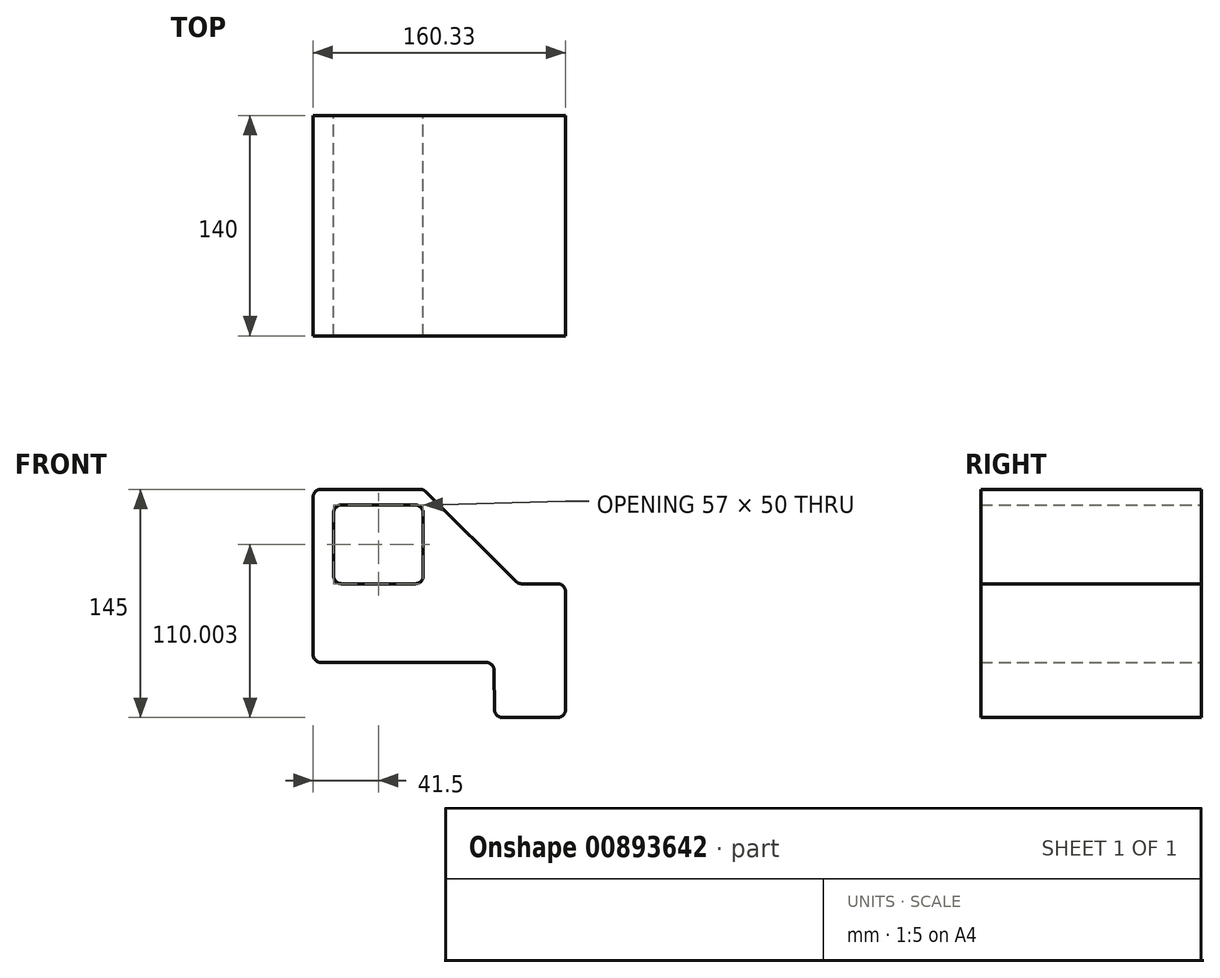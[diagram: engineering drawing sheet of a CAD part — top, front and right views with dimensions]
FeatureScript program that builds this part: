
annotation { "Feature Type Name" : "Feature", "Feature Type Description" : "" }
export const myFeature = defineFeature(function(context is Context, id is Id, definition is map)
    precondition{}
    {
        {
            var Q0;
            Q0=qCreatedBy(makeId("Front.planeOp"),FACE);
            var sketch = newSketch(context, id + "F0", { "sketchPlane" : qUnion([Q0])});
            skLineSegment(sketch, "E0", {"start": v(-70, 32.02) * mm, "end": v(45, 32.02) * mm});
            skLineSegment(sketch, "E1", {"start": v(45.33, -2.98) * mm, "end": v(90.33, -2.98) * mm});
            skLineSegment(sketch, "E2", {"start": v(90.33, -2.98) * mm, "end": v(90.33, 82.02) * mm});
            skLineSegment(sketch, "E3", {"start": v(90.33, 82.02) * mm, "end": v(60.33, 82.02) * mm});
            skLineSegment(sketch, "E4", {"start": v(60.33, 82.02) * mm, "end": v(0, 142.02) * mm});
            skLineSegment(sketch, "E5", {"start": v(0, 142.02) * mm, "end": v(-70, 142.02) * mm});
            skLineSegment(sketch, "E6", {"start": v(-70, 142.02) * mm, "end": v(-70, 32.02) * mm});
            skLineSegment(sketch, "E7", {"start": v(45, 32.02) * mm, "end": v(45.33, -2.98) * mm});
            skSolve(sketch);
        }
        {
            var Q0;
            Q0 = qSketchRegion(id + "F0", true);
            extrude(context, id + "F1", {"entities" : qUnion([Q0]), "endBound" : BoundingType.SYMMETRIC, "depth" : 140 * mm, "offsetDistance" : 25 * mm});
        }
        {
            var Q0;
            Q0=makeQuery(id+"F1.opExtrude","CAP_FACE",FACE,{"disambiguationData":[OSD([sQuery(id+"F0.wireOp",EDGE,"E0"),sQuery(id+"F0.wireOp",EDGE,"E1"),sQuery(id+"F0.wireOp",EDGE,"E2"),sQuery(id+"F0.wireOp",EDGE,"E3"),sQuery(id+"F0.wireOp",EDGE,"E4"),sQuery(id+"F0.wireOp",EDGE,"E5"),sQuery(id+"F0.wireOp",EDGE,"E6"),sQuery(id+"F0.wireOp",EDGE,"E7")])],"isStart":true});
            var sketch = newSketch(context, id + "F2", { "sketchPlane" : qUnion([Q0])});
            skLineSegment(sketch, "E8.bottom", {"start": v(5, 132.02) * mm, "end": v(52, 132.02) * mm});
            skLineSegment(sketch, "E8.top", {"start": v(5, 82.02) * mm, "end": v(52, 82.02) * mm});
            skLineSegment(sketch, "E8.left", {"start": v(0, 127.02) * mm, "end": v(0, 87.02) * mm});
            skLineSegment(sketch, "E8.right", {"start": v(57, 127.02) * mm, "end": v(57, 87.02) * mm});
            skPoint(sketch, "E9.visualSharp", {"position": v(0, 132.02) * mm});
            skArc(sketch, "E9.filletArc", {"start": v(5, 132.02) * mm, "mid": v(1.46, 130.56) * mm, "end": v(0, 127.02) * mm});
            skPoint(sketch, "E10.visualSharp", {"position": v(57, 132.02) * mm});
            skArc(sketch, "E10.filletArc", {"start": v(57, 127.02) * mm, "mid": v(55.54, 130.56) * mm, "end": v(52, 132.02) * mm});
            skPoint(sketch, "E11.visualSharp", {"position": v(57, 82.02) * mm});
            skArc(sketch, "E11.filletArc", {"start": v(52, 82.02) * mm, "mid": v(55.54, 83.49) * mm, "end": v(57, 87.02) * mm});
            skPoint(sketch, "E12.visualSharp", {"position": v(0, 82.02) * mm});
            skArc(sketch, "E12.filletArc", {"start": v(0, 87.02) * mm, "mid": v(1.46, 83.49) * mm, "end": v(5, 82.02) * mm});
            skSolve(sketch);
        }
        {
            var Q0;
            Q0=makeQuery(id+"F2.imprint","IMPRINT",FACE,{"disambiguationData":[TD([[makeQuery(id+"F2.imprint","IMPRINT",EDGE,{"derivedFrom":sQuery(id+"F2.wireOp",EDGE,"E8.bottom")}),-1.0]])]});
            extrude(context, id + "F3", {"entities" : qUnion([Q0]), "operationType" : NewBodyOperationType.REMOVE, "endBound" : BoundingType.THROUGH_ALL, "oppositeDirection" : true, "depth" : 25 * mm, "offsetDistance" : 25 * mm});
        }
        {
            var Q0;
            Q0=makeQuery(id+"F1.opExtrude","SWEPT_EDGE",EDGE,{"disambiguationData":[OSD([sQuery(id+"F0.wireOp",EDGE,"E4"),sQuery(id+"F0.wireOp",EDGE,"E5")])]});
            var Q1;
            Q1=makeQuery(id+"F1.opExtrude","SWEPT_EDGE",EDGE,{"disambiguationData":[OSD([sQuery(id+"F0.wireOp",EDGE,"E3"),sQuery(id+"F0.wireOp",EDGE,"E4")])]});
            var Q2;
            Q2=makeQuery(id+"F1.opExtrude","SWEPT_EDGE",EDGE,{"disambiguationData":[OSD([sQuery(id+"F0.wireOp",EDGE,"E2"),sQuery(id+"F0.wireOp",EDGE,"E3")])]});
            var Q3;
            Q3=makeQuery(id+"F1.opExtrude","SWEPT_EDGE",EDGE,{"disambiguationData":[OSD([sQuery(id+"F0.wireOp",EDGE,"E1"),sQuery(id+"F0.wireOp",EDGE,"E2")])]});
            var Q4;
            Q4=makeQuery(id+"F1.opExtrude","SWEPT_EDGE",EDGE,{"disambiguationData":[OSD([sQuery(id+"F0.wireOp",EDGE,"E1"),sQuery(id+"F0.wireOp",EDGE,"E7")])]});
            var Q5;
            Q5=makeQuery(id+"F1.opExtrude","SWEPT_EDGE",EDGE,{"disambiguationData":[OSD([sQuery(id+"F0.wireOp",EDGE,"E0"),sQuery(id+"F0.wireOp",EDGE,"E7")])]});
            var Q6;
            Q6=makeQuery(id+"F1.opExtrude","SWEPT_EDGE",EDGE,{"disambiguationData":[OSD([sQuery(id+"F0.wireOp",EDGE,"E0"),sQuery(id+"F0.wireOp",EDGE,"E6")])]});
            var Q7;
            Q7=makeQuery(id+"F1.opExtrude","SWEPT_EDGE",EDGE,{"disambiguationData":[OSD([sQuery(id+"F0.wireOp",EDGE,"E5"),sQuery(id+"F0.wireOp",EDGE,"E6")])]});
            fillet(context, id + "F4", {"entities" : qUnion([Q0, Q1, Q2, Q3, Q4, Q5, Q6, Q7]), "radius" : 5 * mm, "tangentPropagation" : true, "allowEdgeOverflow" : false});
        }
    });
